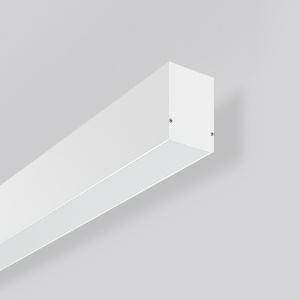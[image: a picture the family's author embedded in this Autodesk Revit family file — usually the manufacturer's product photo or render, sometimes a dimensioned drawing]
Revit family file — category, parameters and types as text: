
# Revit family: less_is_more_50_312605_002_76_b2a3
name_source: partatom
category: Lighting Fixtures
units: mm (PartAtom-declared; Revit-internal decimal feet)

## family parameters
Cut with Voids When Loaded = No
Host = Face
Light Source = No
Part Type = Normal
Room Calculation Point = No
Round Connector Dimension = Use Diameter
Shared = No

## types (1)
- LESS IS MORE 50 (1 x LED Modul 830, 1100 lm, 3000)
    Apparent Load = 9 VA
    CIE Flux Codes = 48 80 96 100 100
    Color Rendering = 80
    Color Temperature = 3000
    Default Elevation = 1800 mm
    Description = Series: LESS IS MORE 50
Linear wall luminaires. Housing: extruded aluminium profile, powder-coated. End cap aluminium powder-coated. Diffuser made of non-yellowing plastic (PMMA), opal. Direct light emission. Suitable for Wall (surface). LED unit with integrated converter interchangeable and removable. Suitable for through-wiring. With sensors or as a safety luminaire on request. 
Colour: traffic white, matt (RAL 9016)
Length: 847 mm
Width: 67 mm
Height: 75 mm
Lamp: LED
Socket: without socket
Colour temperature: 3000K
Colour rendering index (CRI): 80
System power: 9 W
Rated luminous flux: 1100 lm
Luminous efficiency: 122 lm/W
Control gear: Converter, dimmable, DALI
Protection class: I
Type of protection: IP 20
    Height = 75 mm
    Lamp = 1 x LED Modul 830
    Lamp Light Flux = 1100 lm
    Lamp count = 1
    Length = 847 mm
    Lifetime = 50000 h
    Luminous efficacy = 122 lm/W
    Manufacturer = RZB
    ModVariant = No
    Model = 312605.002.76
    Mounting Place = Wall
    Mounting Type = Surface mounted
    Number of Poles = 1
    OnlyDefault = Yes
    Power Factor = 1
    Product Name = LESS IS MORE 50
    Product group = Surface mounted LED linear luminaires
    ProductGroupID = 2007
    Protection Class = Protection class I
    Protection Degree = IP 20
    RLX_Detail_Level = 1
    RLX_Emergency_Light_Flux = 0 lm
    RLX_Emergency_Type = 0
    RLX_Emergency_Type_DB = No
    RlxData = <blob elided: 35165 chars, md5=48c21cc2>
    Socket = socket
    Standby Power = 0 W
    System Light Flux = 1100 lm
    System Power = 9 W
    Type Comments = Product without accessories
    Type Image = 312606.002.jpg
    URL = http://relux.com
    VarID = ---
    Voltage = 0 V
    Weight = 0.00 kg
    Width = 67 mm

## geometry (parser evidence)
native form markers: Blend x4, Sweep x11
no freeform markers — native parametric forms only
